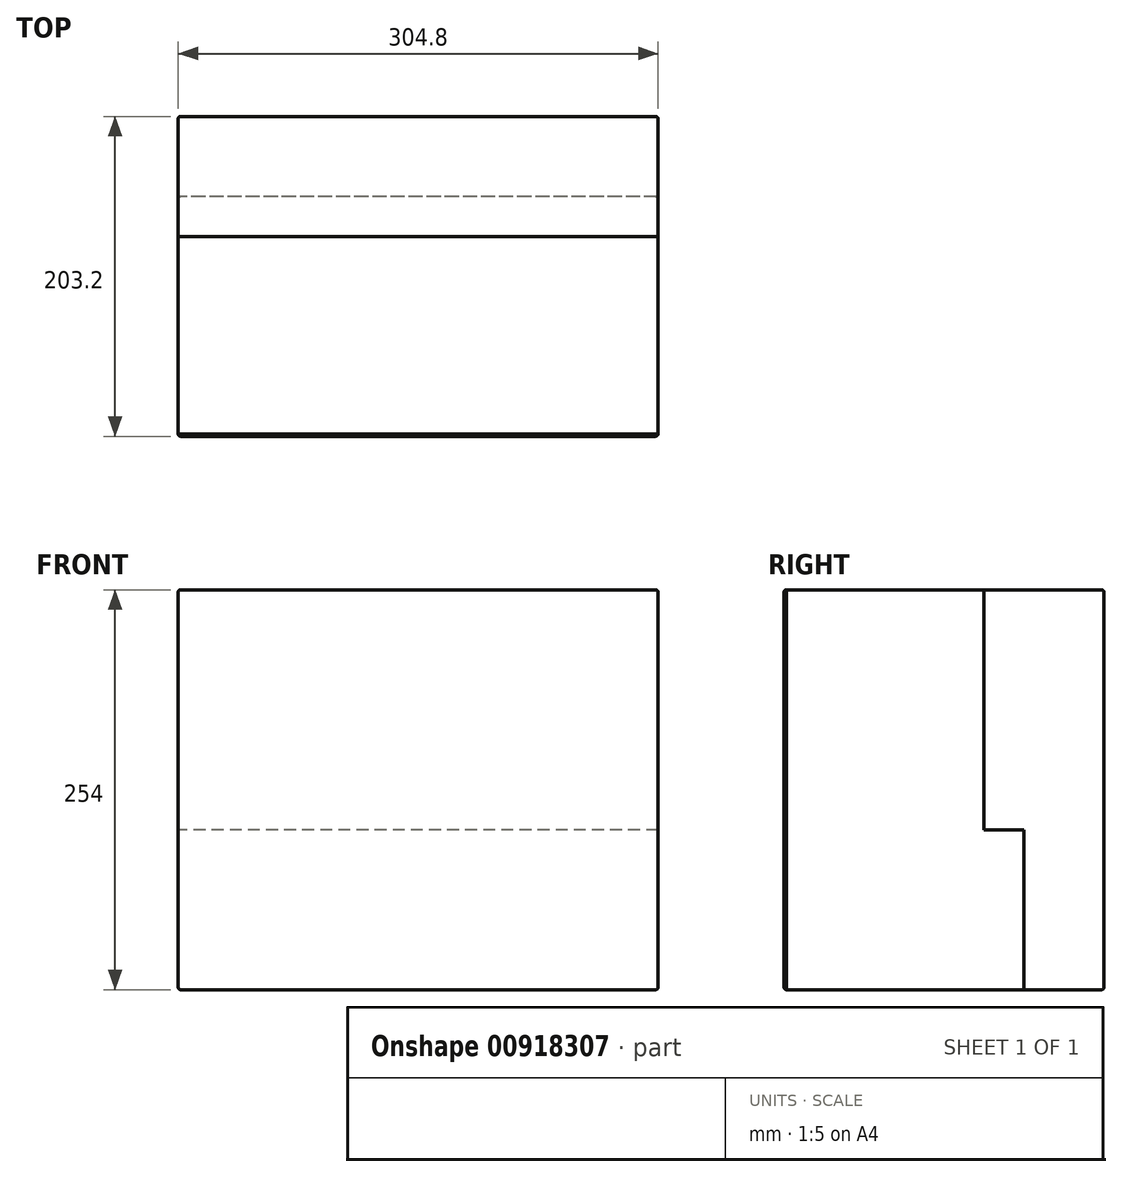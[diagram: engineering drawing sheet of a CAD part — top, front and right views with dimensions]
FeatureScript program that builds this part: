
annotation { "Feature Type Name" : "Feature", "Feature Type Description" : "" }
export const myFeature = defineFeature(function(context is Context, id is Id, definition is map)
    precondition{}
    {
        {
            var Q0;
            Q0=qCreatedBy(makeId("Front.planeOp"),FACE);
            var sketch = newSketch(context, id + "F0", { "sketchPlane" : qUnion([Q0])});
            skLineSegment(sketch, "E0.bottom", {"start": v(152.4, 127) * mm, "end": v(-152.4, 127) * mm});
            skLineSegment(sketch, "E0.top", {"start": v(152.4, -127) * mm, "end": v(-152.4, -127) * mm});
            skLineSegment(sketch, "E0.left", {"start": v(152.4, 127) * mm, "end": v(152.4, -127) * mm});
            skLineSegment(sketch, "E0.right", {"start": v(-152.4, 127) * mm, "end": v(-152.4, -127) * mm});
            skPoint(sketch, "E0.middle", {"position": v(0, 0) * mm});
            skSolve(sketch);
        }
        {
            var Q0;
            Q0=makeQuery(id+"F0.imprint","IMPRINT",FACE,{"disambiguationData":[TD([[makeQuery(id+"F0.imprint","IMPRINT",EDGE,{"derivedFrom":sQuery(id+"F0.wireOp",EDGE,"E0.bottom")}),1.0]])]});
            extrude(context, id + "F1", {"entities" : qUnion([Q0]), "endBound" : BoundingType.SYMMETRIC, "depth" : 203.2 * mm, "offsetDistance" : 25.4 * mm});
        }
        {
            var Q0;
            Q0=makeQuery(id+"F1.opExtrude","CAP_FACE",FACE,{"disambiguationData":[OSD([sQuery(id+"F0.wireOp",EDGE,"E0.bottom"),sQuery(id+"F0.wireOp",EDGE,"E0.top"),sQuery(id+"F0.wireOp",EDGE,"E0.left"),sQuery(id+"F0.wireOp",EDGE,"E0.right")])],"isStart":false});
            var Q1;
            Q1=makeQuery(id+"F1.opExtrude","CAP_FACE",FACE,{"disambiguationData":[OSD([sQuery(id+"F0.wireOp",EDGE,"E0.bottom"),sQuery(id+"F0.wireOp",EDGE,"E0.top"),sQuery(id+"F0.wireOp",EDGE,"E0.left"),sQuery(id+"F0.wireOp",EDGE,"E0.right")])],"isStart":true});
            var Q2;
            Q2=makeQuery(id+"F1.opExtrude","SWEPT_FACE",FACE,{"disambiguationData":[OSD([sQuery(id+"F0.wireOp",EDGE,"E0.bottom")])]});
            var Q3;
            Q3=makeQuery(id+"F1.opExtrude","SWEPT_FACE",FACE,{"disambiguationData":[OSD([sQuery(id+"F0.wireOp",EDGE,"E0.top")])]});
            fillet(context, id + "F2", {"entities" : qUnion([Q0, Q1, Q2, Q3]), "radius" : 1.52 * mm, "tangentPropagation" : true, "allowEdgeOverflow" : false});
        }
        {
            var Q0;
            Q0=qCreatedBy(makeId("Right.planeOp"),FACE);
            var sketch = newSketch(context, id + "F3", { "sketchPlane" : qUnion([Q0])});
            skLineSegment(sketch, "E1", {"start": v(-100.08, 127) * mm, "end": v(-100.08, -127) * mm});
            skLineSegment(sketch, "E2", {"start": v(-100.08, -127) * mm, "end": v(50.8, -127) * mm});
            skLineSegment(sketch, "E3", {"start": v(50.8, -127) * mm, "end": v(50.8, -25.4) * mm});
            skLineSegment(sketch, "E4", {"start": v(50.8, -25.4) * mm, "end": v(25.4, -25.4) * mm});
            skLineSegment(sketch, "E5", {"start": v(25.4, -25.4) * mm, "end": v(25.4, 127) * mm});
            skLineSegment(sketch, "E6", {"start": v(25.4, 127) * mm, "end": v(-100.08, 127) * mm});
            skSolve(sketch);
        }
        {
            var Q0;
            Q0 = qSketchRegion(id + "F3", true);
            extrude(context, id + "F4", {"entities" : qUnion([Q0]), "endBound" : BoundingType.SYMMETRIC, "depth" : 304.8 * mm, "offsetDistance" : 25.4 * mm});
        }
        {
            var Q0;
            Q0=makeQuery(id+"F4.opExtrude","SWEPT_BODY",BODY,{"disambiguationData":[OSD([sQuery(id+"F3.wireOp",EDGE,"E1"),sQuery(id+"F3.wireOp",EDGE,"E2"),sQuery(id+"F3.wireOp",EDGE,"E3"),sQuery(id+"F3.wireOp",EDGE,"E4"),sQuery(id+"F3.wireOp",EDGE,"E5"),sQuery(id+"F3.wireOp",EDGE,"E6")])]});
            var Q1;
            Q1=makeQuery(id+"F1.opExtrude","SWEPT_BODY",BODY,{"disambiguationData":[OSD([sQuery(id+"F0.wireOp",EDGE,"E0.bottom"),sQuery(id+"F0.wireOp",EDGE,"E0.top"),sQuery(id+"F0.wireOp",EDGE,"E0.left"),sQuery(id+"F0.wireOp",EDGE,"E0.right")])]});
            booleanBodies(context, id + "F5", {"operationType" : BooleanOperationType.SUBTRACTION, "tools" : qUnion([Q0]), "targets" : qUnion([Q1]), "keepTools" : true});
        }
        {
            var Q0;
            Q0=makeQuery(id+"F4.opExtrude","CAP_EDGE",EDGE,{"disambiguationData":[OSD([sQuery(id+"F3.wireOp",EDGE,"E6")])],"isStart":false});
            var Q1;
            Q1=makeQuery(id+"F4.opExtrude","CAP_EDGE",EDGE,{"disambiguationData":[OSD([sQuery(id+"F3.wireOp",EDGE,"E2")])],"isStart":false});
            var Q2;
            Q2=makeQuery(id+"F4.opExtrude","CAP_EDGE",EDGE,{"disambiguationData":[OSD([sQuery(id+"F3.wireOp",EDGE,"E2")])],"isStart":true});
            var Q3;
            Q3=makeQuery(id+"F4.opExtrude","CAP_EDGE",EDGE,{"disambiguationData":[OSD([sQuery(id+"F3.wireOp",EDGE,"E6")])],"isStart":true});
            fillet(context, id + "F6", {"entities" : qUnion([Q0, Q1, Q2, Q3]), "radius" : 1.52 * mm, "tangentPropagation" : true, "allowEdgeOverflow" : false});
        }
    });
